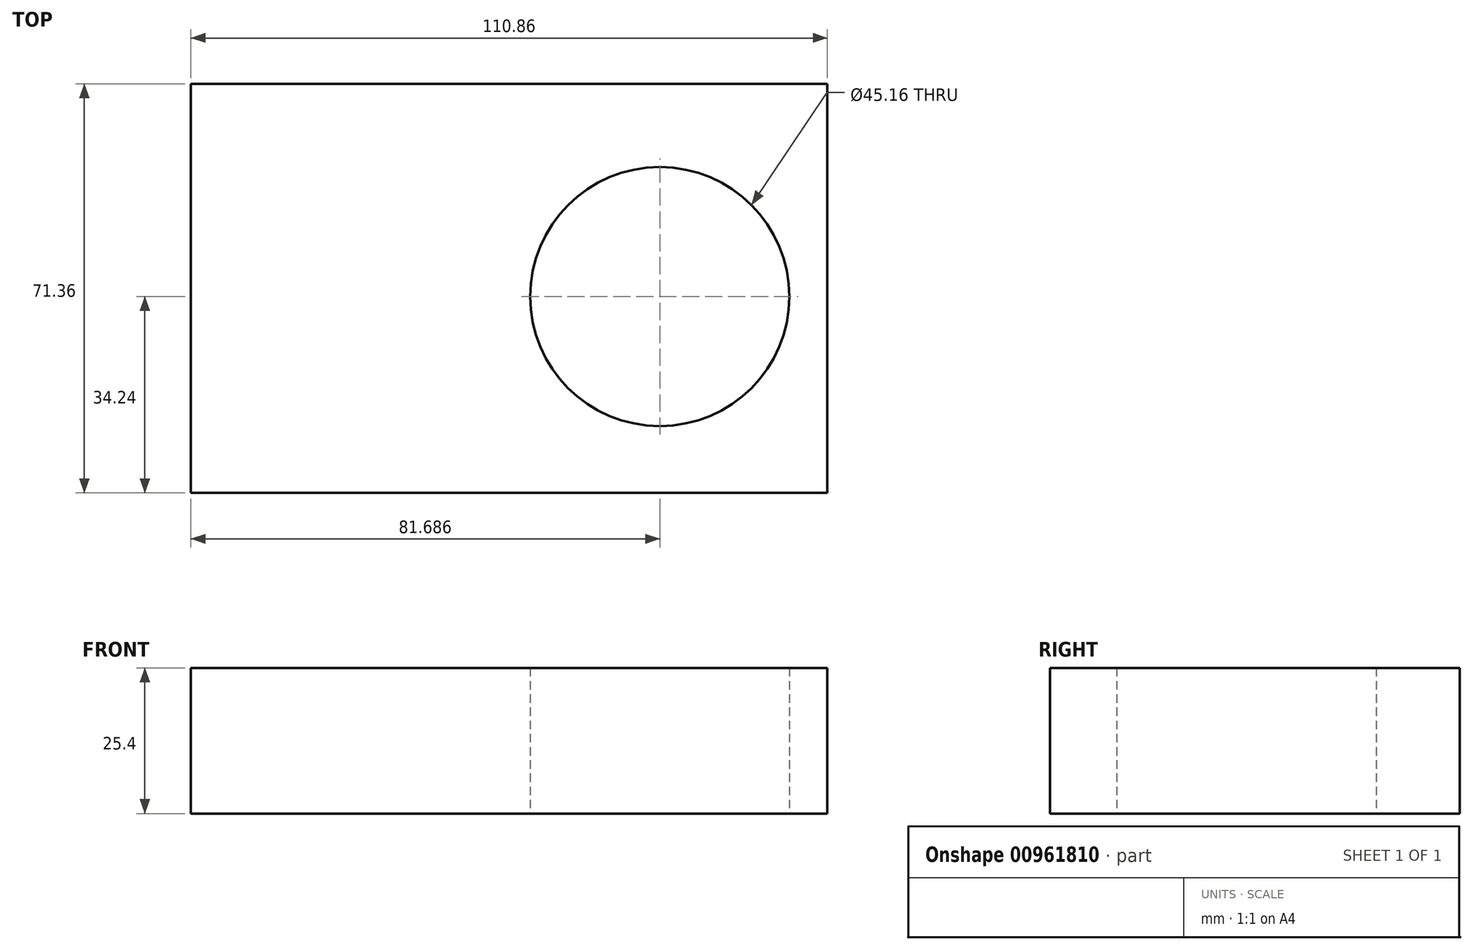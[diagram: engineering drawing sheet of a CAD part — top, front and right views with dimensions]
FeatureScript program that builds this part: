
annotation { "Feature Type Name" : "Feature", "Feature Type Description" : "" }
export const myFeature = defineFeature(function(context is Context, id is Id, definition is map)
    precondition{}
    {
        {
            var Q0;
            Q0=qCreatedBy(makeId("Top.planeOp"),FACE);
            var sketch = newSketch(context, id + "F0", { "sketchPlane" : qUnion([Q0])});
            skLineSegment(sketch, "E0.bottom", {"start": v(-48.02, 37.12) * mm, "end": v(62.84, 37.12) * mm});
            skLineSegment(sketch, "E0.top", {"start": v(-48.02, -34.24) * mm, "end": v(62.84, -34.24) * mm});
            skLineSegment(sketch, "E0.left", {"start": v(-48.02, 37.12) * mm, "end": v(-48.02, -34.24) * mm});
            skLineSegment(sketch, "E0.right", {"start": v(62.84, 37.12) * mm, "end": v(62.84, -34.24) * mm});
            skSolve(sketch);
        }
        {
            var Q0;
            Q0=qCreatedBy(makeId("Top.planeOp"),FACE);
            var sketch = newSketch(context, id + "F1", { "sketchPlane" : qUnion([Q0])});
            skCircle(sketch, "E1", {"center": v(33.67, 0) * mm, "radius": 22.58 * mm});
            skSolve(sketch);
        }
        {
            var Q0;
            Q0=makeQuery(id+"F0.imprint","IMPRINT",FACE,{"disambiguationData":[TD([[makeQuery(id+"F0.imprint","IMPRINT",EDGE,{"derivedFrom":sQuery(id+"F0.wireOp",EDGE,"E0.bottom")}),-1.0]])]});
            var Q1;
            Q1=makeQuery(id+"F1.imprint","IMPRINT",FACE,{"disambiguationData":[TD([[makeQuery(id+"F1.imprint","IMPRINT",EDGE,{"derivedFrom":sQuery(id+"F1.wireOp",EDGE,"E1")}),1.0]])]});
            extrude(context, id + "F2", {"entities" : qUnion([Q0, Q1]), "depth" : 25.4 * mm, "offsetDistance" : 25.4 * mm});
        }
        {
            var Q0;
            Q0=makeQuery(id+"F2.opExtrude","SWEPT_BODY",BODY,{"disambiguationData":[OSD([sQuery(id+"F1.wireOp",EDGE,"E1")])]});
            var Q1;
            Q1=makeQuery(id+"F2.opExtrude","SWEPT_BODY",BODY,{"disambiguationData":[OSD([sQuery(id+"F0.wireOp",EDGE,"E0.bottom"),sQuery(id+"F0.wireOp",EDGE,"E0.top"),sQuery(id+"F0.wireOp",EDGE,"E0.left"),sQuery(id+"F0.wireOp",EDGE,"E0.right")])]});
            booleanBodies(context, id + "F3", {"operationType" : BooleanOperationType.SUBTRACTION, "tools" : qUnion([Q0]), "targets" : qUnion([Q1])});
        }
    });
